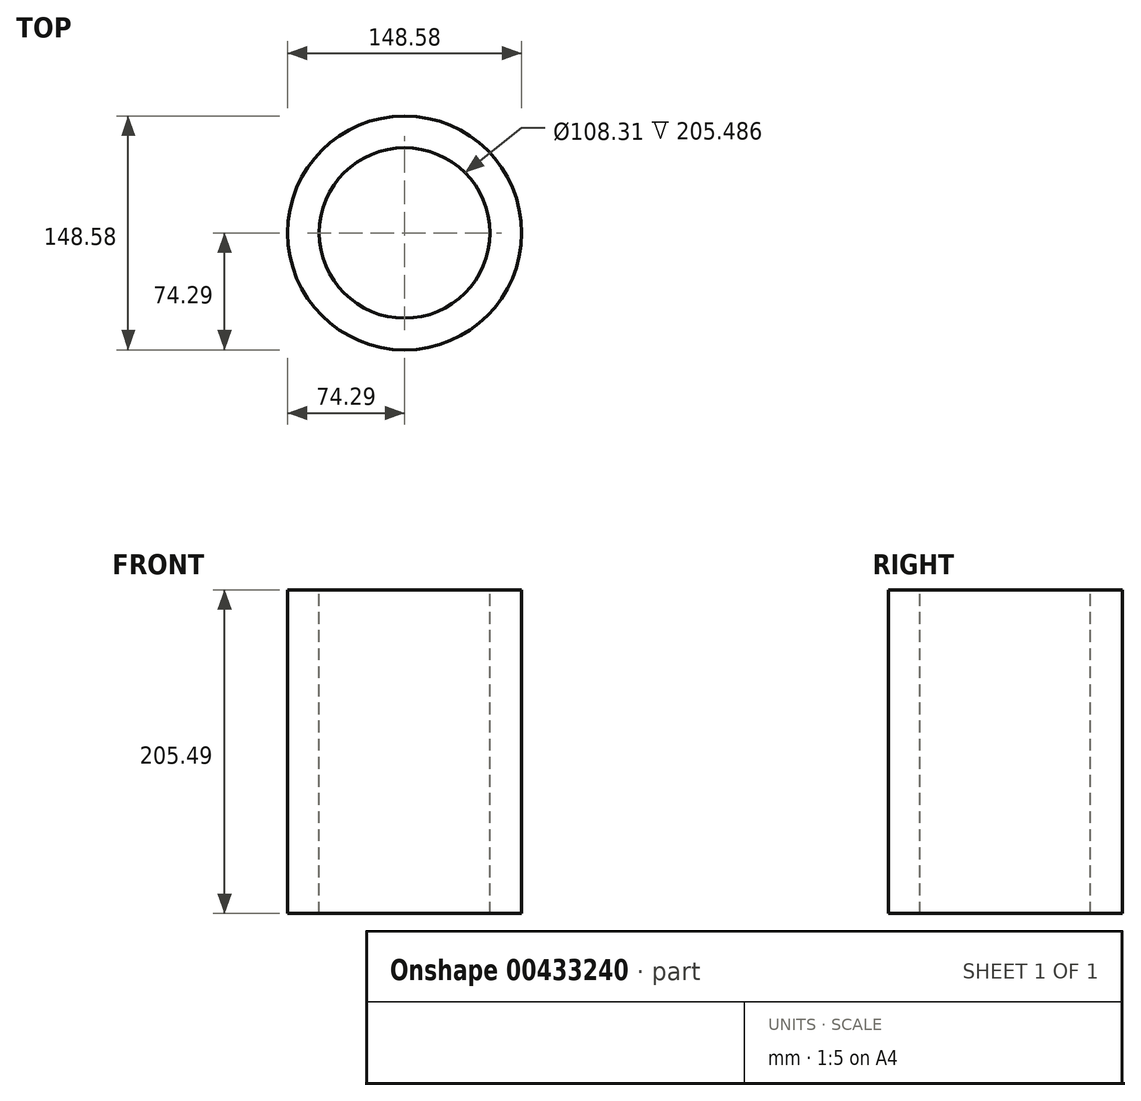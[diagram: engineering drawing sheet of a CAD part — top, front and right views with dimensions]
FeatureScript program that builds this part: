
annotation { "Feature Type Name" : "Feature", "Feature Type Description" : "" }
export const myFeature = defineFeature(function(context is Context, id is Id, definition is map)
    precondition{}
    {
        {
            var Q0;
            Q0=qCreatedBy(makeId("Top.planeOp"),FACE);
            var sketch = newSketch(context, id + "F0", { "sketchPlane" : qUnion([Q0])});
            skCircle(sketch, "E0", {"center": v(0, 0) * mm, "radius": 74.29 * mm});
            skSolve(sketch);
        }
        {
            var Q0;
            Q0=makeQuery(id+"F0.imprint","IMPRINT",FACE,{"disambiguationData":[TD([[makeQuery(id+"F0.imprint","IMPRINT",EDGE,{"derivedFrom":sQuery(id+"F0.wireOp",EDGE,"E0")}),1.0]])]});
            extrude(context, id + "F1", {"entities" : qUnion([Q0]), "depth" : 151.9 * mm});
        }
        {
            var Q0;
            Q0=makeQuery(id+"F1.opExtrude","CAP_FACE",FACE,{"disambiguationData":[OSD([sQuery(id+"F0.wireOp",EDGE,"E0")])],"isStart":false});
            extrude(context, id + "F2", {"entities" : qUnion([Q0]), "operationType" : NewBodyOperationType.ADD, "depth" : 53.6 * mm});
        }
        {
            var Q0;
            Q0=makeQuery(id+"F2.opExtrude","CAP_FACE",FACE,{"disambiguationData":[OSD([sQuery(id+"F0.wireOp",EDGE,"E0")])],"isStart":false});
            var sketch = newSketch(context, id + "F3", { "sketchPlane" : qUnion([Q0])});
            skCircle(sketch, "E1", {"center": v(0, 0) * mm, "radius": 54.15 * mm});
            skSolve(sketch);
        }
        {
            var Q0;
            Q0=makeQuery(id+"F3.imprint","IMPRINT",FACE,{"disambiguationData":[TD([[makeQuery(id+"F3.imprint","IMPRINT",EDGE,{"derivedFrom":sQuery(id+"F3.wireOp",EDGE,"E1")}),1.0]])]});
            extrude(context, id + "F4", {"entities" : qUnion([Q0]), "operationType" : NewBodyOperationType.REMOVE, "oppositeDirection" : true, "depth" : 195.58 * mm});
        }
        {
            var Q0;
            Q0=makeQuery(id+"F4.boolean.opBoolean","COPY",FACE,{"derivedFrom":makeQuery(id+"F4.opExtrude","CAP_FACE",FACE,{"disambiguationData":[OSD([sQuery(id+"F3.wireOp",EDGE,"E1")])],"isStart":false})});
            var Q1;
            Q1 = qSketchRegion(id + "FOXXwrxYUWyvhoJ_1", true);
            extrude(context, id + "F5", {"entities" : qUnion([Q0, Q1]), "operationType" : NewBodyOperationType.REMOVE, "oppositeDirection" : true, "depth" : 92.2 * mm});
        }
    });
